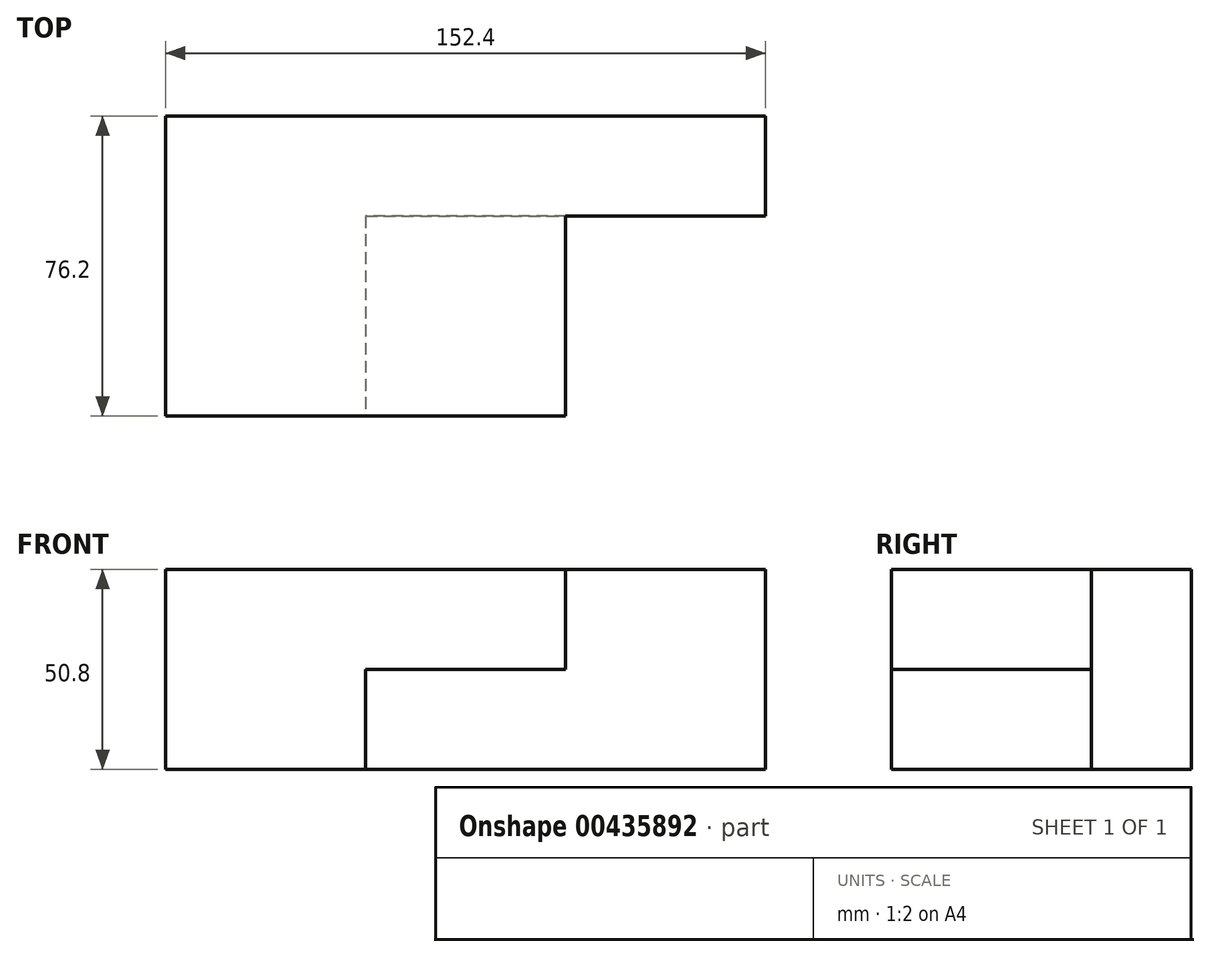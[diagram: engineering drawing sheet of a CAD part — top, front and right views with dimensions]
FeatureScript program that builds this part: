
annotation { "Feature Type Name" : "Feature", "Feature Type Description" : "" }
export const myFeature = defineFeature(function(context is Context, id is Id, definition is map)
    precondition{}
    {
        {
            var Q0;
            Q0=qCreatedBy(makeId("Front.planeOp"),FACE);
            var sketch = newSketch(context, id + "F0", { "sketchPlane" : qUnion([Q0])});
            skLineSegment(sketch, "E0", {"start": v(0, 0) * mm, "end": v(152.4, 0) * mm});
            skLineSegment(sketch, "E1", {"start": v(0, 0) * mm, "end": v(0, 50.8) * mm});
            skLineSegment(sketch, "E2", {"start": v(0, 50.8) * mm, "end": v(152.4, 50.8) * mm});
            skLineSegment(sketch, "E3", {"start": v(152.4, 50.8) * mm, "end": v(152.4, 0) * mm});
            skSolve(sketch);
        }
        {
            var Q0;
            Q0=makeQuery(id+"F0.imprint","IMPRINT",FACE,{"disambiguationData":[TD([[makeQuery(id+"F0.imprint","IMPRINT",EDGE,{"derivedFrom":sQuery(id+"F0.wireOp",EDGE,"E0")}),1.0]])]});
            extrude(context, id + "F1", {"entities" : qUnion([Q0]), "oppositeDirection" : true, "depth" : 76.2 * mm});
        }
        {
            var Q0;
            Q0=qCreatedBy(makeId("Front.planeOp"),FACE);
            var sketch = newSketch(context, id + "F2", { "sketchPlane" : qUnion([Q0])});
            skLineSegment(sketch, "E4", {"start": v(0, 0) * mm, "end": v(50.8, 0) * mm});
            skLineSegment(sketch, "E5", {"start": v(50.8, 0) * mm, "end": v(50.8, 25.4) * mm});
            skLineSegment(sketch, "E6", {"start": v(50.8, 25.4) * mm, "end": v(101.6, 25.4) * mm});
            skLineSegment(sketch, "E7", {"start": v(101.6, 25.4) * mm, "end": v(101.6, 50.8) * mm});
            skLineSegment(sketch, "E8", {"start": v(101.6, 50.8) * mm, "end": v(152.4, 50.8) * mm});
            skLineSegment(sketch, "E9", {"start": v(152.4, 50.8) * mm, "end": v(152.4, 0) * mm});
            skLineSegment(sketch, "E10", {"start": v(152.4, 0) * mm, "end": v(50.8, 0) * mm});
            skSolve(sketch);
        }
        {
            var Q0;
            Q0=makeQuery(id+"F2.imprint","IMPRINT",FACE,{"disambiguationData":[TD([[makeQuery(id+"F2.imprint","IMPRINT",EDGE,{"derivedFrom":sQuery(id+"F2.wireOp",EDGE,"E5")}),-1.0]])]});
            extrude(context, id + "F3", {"entities" : qUnion([Q0]), "operationType" : NewBodyOperationType.REMOVE, "oppositeDirection" : true, "depth" : 50.8 * mm});
        }
    });
